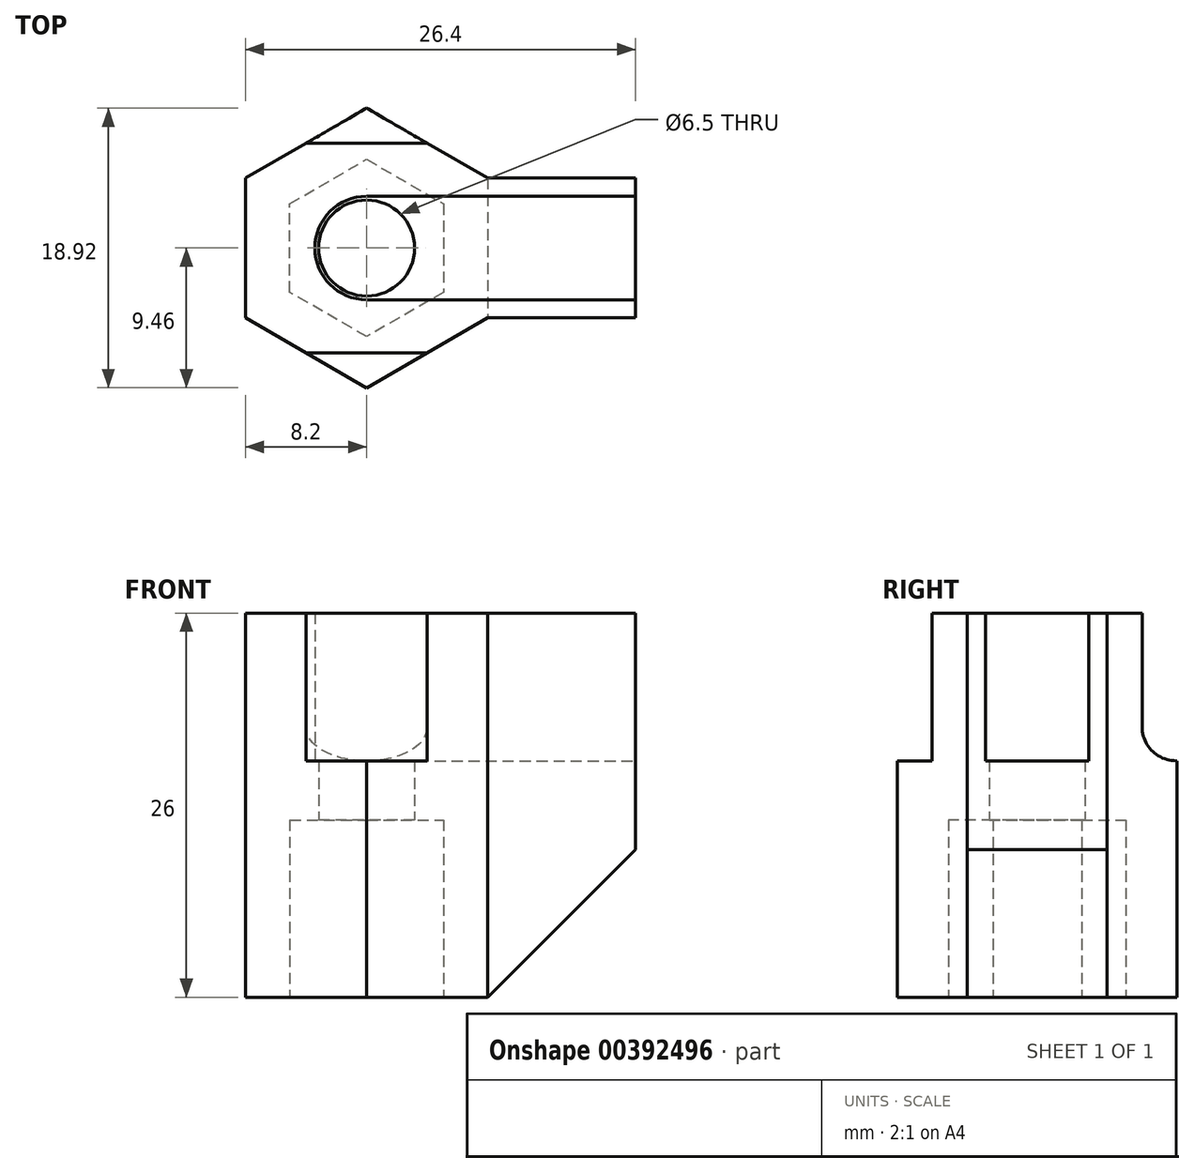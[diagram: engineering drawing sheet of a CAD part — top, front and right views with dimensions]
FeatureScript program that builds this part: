
annotation { "Feature Type Name" : "Feature", "Feature Type Description" : "" }
export const myFeature = defineFeature(function(context is Context, id is Id, definition is map)
    precondition{}
    {
        {
            var Q0;
            Q0=qCreatedBy(makeId("Top.planeOp"),FACE);
            var sketch = newSketch(context, id + "F0", { "sketchPlane" : qUnion([Q0])});
            skCircle(sketch, "E0.cCircle", {"center": v(0, 0) * mm, "radius": 6 * mm, "construction": true});
            skLineSegment(sketch, "E0.0", {"start": v(0, 6) * mm, "end": v(5.2, 3) * mm});
            skLineSegment(sketch, "E0.1", {"start": v(5.2, 3) * mm, "end": v(5.2, -3) * mm});
            skLineSegment(sketch, "E0.2", {"start": v(5.2, -3) * mm, "end": v(0, -6) * mm});
            skLineSegment(sketch, "E0.3", {"start": v(0, -6) * mm, "end": v(-5.2, -3) * mm});
            skLineSegment(sketch, "E0.4", {"start": v(-5.2, -3) * mm, "end": v(-5.2, 3) * mm});
            skLineSegment(sketch, "E0.5", {"start": v(-5.2, 3) * mm, "end": v(0, 6) * mm});
            skLineSegment(sketch, "E1.0", {"start": v(-8.2, -4.73) * mm, "end": v(-8.2, 4.73) * mm});
            skLineSegment(sketch, "E1.1", {"start": v(0, 9.46) * mm, "end": v(8.2, 4.73) * mm});
            skLineSegment(sketch, "E1.2", {"start": v(8.2, 4.73) * mm, "end": v(8.2, -4.73) * mm});
            skLineSegment(sketch, "E1.3", {"start": v(-8.2, 4.73) * mm, "end": v(0, 9.46) * mm});
            skLineSegment(sketch, "E1.4", {"start": v(8.2, -4.73) * mm, "end": v(0, -9.46) * mm});
            skLineSegment(sketch, "E1.5", {"start": v(0, -9.46) * mm, "end": v(-8.2, -4.73) * mm});
            skSolve(sketch);
        }
        {
            var Q0;
            Q0=makeQuery(id+"F0.imprint","IMPRINT",FACE,{"disambiguationData":[TD([[makeQuery(id+"F0.imprint","IMPRINT",EDGE,{"derivedFrom":sQuery(id+"F0.wireOp",EDGE,"E0.0")}),1.0]])]});
            extrude(context, id + "F1", {"entities" : qUnion([Q0]), "depth" : 12 * mm});
        }
        {
            var Q0;
            Q0=makeQuery(id+"F1.opExtrude","SWEPT_FACE",FACE,{"disambiguationData":[OSD([sQuery(id+"F0.wireOp",EDGE,"E1.2")])]});
            extrude(context, id + "F2", {"entities" : qUnion([Q0]), "operationType" : NewBodyOperationType.ADD, "depth" : 10 * mm});
        }
        {
            var Q0;
            {var subQ0=sQuery(id+"F0.wireOp",EDGE,"E1.2");Q0=makeQuery(id+"F2.opExtrude","CAP_EDGE",EDGE,{"disambiguationData":[OSD([subQ0]),TDD([makeQuery(id+"F1.opExtrude","CAP_EDGE",EDGE,{"disambiguationData":[OSD([subQ0])],"isStart":true})])],"isStart":false});}
            chamfer(context, id + "F3", {"entities" : qUnion([Q0]), "width" : 10 * mm, "tangentPropagation" : true});
        }
        {
            var Q0;
            {var subQ0=sQuery(id+"F0.wireOp",EDGE,"E1.2");Q0=makeQuery(id+"F2.boolean.opBoolean","MERGE",FACE,{"derivedFrom":[makeQuery(id+"F1.opExtrude","CAP_FACE",FACE,{"disambiguationData":[OSD([sQuery(id+"F0.wireOp",EDGE,"E0.0"),sQuery(id+"F0.wireOp",EDGE,"E0.1"),sQuery(id+"F0.wireOp",EDGE,"E0.2"),sQuery(id+"F0.wireOp",EDGE,"E0.3"),sQuery(id+"F0.wireOp",EDGE,"E0.4"),sQuery(id+"F0.wireOp",EDGE,"E0.5"),sQuery(id+"F0.wireOp",EDGE,"E1.0"),sQuery(id+"F0.wireOp",EDGE,"E1.1"),subQ0,sQuery(id+"F0.wireOp",EDGE,"E1.3"),sQuery(id+"F0.wireOp",EDGE,"E1.4"),sQuery(id+"F0.wireOp",EDGE,"E1.5")])],"isStart":false}),makeQuery(id+"F2.opExtrude","SWEPT_FACE",FACE,{"disambiguationData":[OSD([subQ0]),TDD([makeQuery(id+"F1.opExtrude","CAP_EDGE",EDGE,{"disambiguationData":[OSD([subQ0])],"isStart":false})])]})]});}
            var sketch = newSketch(context, id + "F4", { "sketchPlane" : qUnion([Q0])});
            skCircle(sketch, "E2", {"center": v(0, 0) * mm, "radius": 3.25 * mm});
            skSolve(sketch);
        }
        {
            var Q0;
            Q0=makeQuery(id+"F4.imprint","IMPRINT",FACE,{"disambiguationData":[TD([[makeQuery(id+"F4.imprint","IMPRINT",EDGE,{"derivedFrom":sQuery(id+"F4.wireOp",EDGE,"E2")}),-1.0]])]});
            var Q1;
            Q1=makeQuery(id+"F4.imprint","IMPRINT",FACE,{"disambiguationData":[TD([[makeQuery(id+"F4.imprint","IMPRINT",EDGE,{"derivedFrom":makeQuery(id+"F1.opExtrude","CAP_EDGE",EDGE,{"disambiguationData":[OSD([sQuery(id+"F0.wireOp",EDGE,"E0.0")])],"isStart":false})}),1.0]])]});
            extrude(context, id + "F5", {"entities" : qUnion([Q0, Q1]), "operationType" : NewBodyOperationType.ADD, "depth" : 4 * mm});
        }
        {
            var Q0;
            Q0=makeQuery(id+"F5.opExtrude","CAP_FACE",FACE,{"disambiguationData":[OSD([sQuery(id+"F0.wireOp",EDGE,"E1.0"),sQuery(id+"F0.wireOp",EDGE,"E1.1"),sQuery(id+"F0.wireOp",EDGE,"E1.2"),sQuery(id+"F0.wireOp",EDGE,"E1.3"),sQuery(id+"F0.wireOp",EDGE,"E1.4"),sQuery(id+"F0.wireOp",EDGE,"E1.5"),sQuery(id+"F4.wireOp",EDGE,"E2")])],"isStart":false});
            var sketch = newSketch(context, id + "F6", { "sketchPlane" : qUnion([Q0])});
            skArc(sketch, "E3", {"start": v(0, 3.5) * mm, "mid": v(-3.5, 0) * mm, "end": v(0, -3.5) * mm});
            skLineSegment(sketch, "E4", {"start": v(0, 3.5) * mm, "end": v(18.2, 3.5) * mm});
            skLineSegment(sketch, "E5", {"start": v(0, -3.5) * mm, "end": v(18.2, -3.5) * mm});
            skLineSegment(sketch, "E6", {"start": v(-4.1, -7.1) * mm, "end": v(4.1, -7.1) * mm});
            skLineSegment(sketch, "E7", {"start": v(-4.1, 7.1) * mm, "end": v(4.1, 7.1) * mm});
            skSolve(sketch);
        }
        {
            var Q0;
            Q0=makeQuery(id+"F6.imprint","IMPRINT",FACE,{"disambiguationData":[TD([[makeQuery(id+"F6.imprint","IMPRINT",EDGE,{"derivedFrom":sQuery(id+"F6.wireOp",EDGE,"E3")}),-1.0]])]});
            extrude(context, id + "F7", {"entities" : qUnion([Q0]), "operationType" : NewBodyOperationType.ADD, "depth" : 10 * mm});
        }
        {
            var Q0;
            Q0=makeQuery(id+"F7.opExtrude","CAP_EDGE",EDGE,{"disambiguationData":[OSD([sQuery(id+"F6.wireOp",EDGE,"E6")])],"isStart":true});
            var Q1;
            Q1=makeQuery(id+"F7.opExtrude","CAP_EDGE",EDGE,{"disambiguationData":[OSD([sQuery(id+"F6.wireOp",EDGE,"E7")])],"isStart":true});
            fillet(context, id + "F8", {"entities" : qUnion([Q0, Q1]), "radius" : 2.3 * mm, "tangentPropagation" : true, "allowEdgeOverflow" : false});
        }
    });
